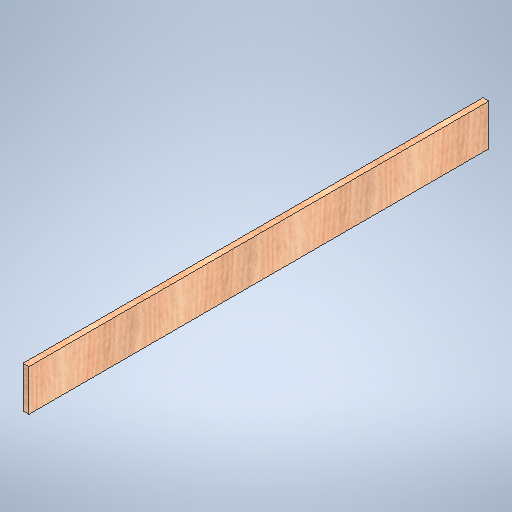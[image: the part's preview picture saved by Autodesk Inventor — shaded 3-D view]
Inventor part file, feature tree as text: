
AUTODESK INVENTOR PART (.ipt)
format: ipt  version: 2025.1 (Build 291241020, 241B)  size: 320,000 bytes
history: native  units: in
note: dims shown in document units (in); Inventor stores cm internally (conversion verified against a paired STEP export)
features: extrude x1, sketch x1
ambient origin geometry x8: Origin, YZ Plane, XZ Plane, XY Plane, X Axis, Y Axis, Z Axis, Center Point
bodies: Solid1 (feature_tree)
feature tree (2):
  extrude  "Extrusion1"  Depth=0.5in TaperAngle=0.0deg
  sketch  "Sketch1"  dims[d1=39.0in d2=0.5in d3=0.0in d4=3.5in]
